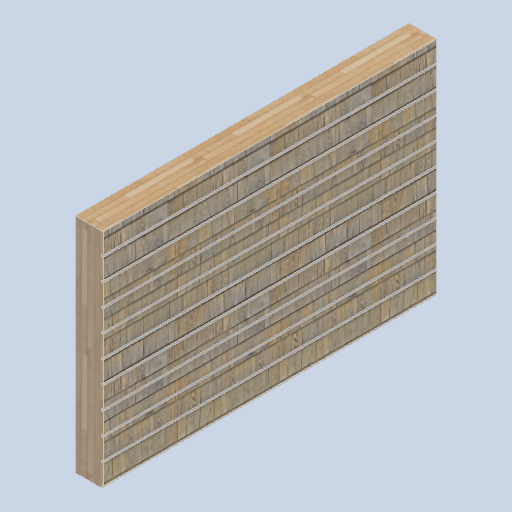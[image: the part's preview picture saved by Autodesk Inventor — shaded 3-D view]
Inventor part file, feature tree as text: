
AUTODESK INVENTOR PART (.ipt)
format: ipt  version: 2024.2 (Build 282272000, 272)  size: 367,616 bytes
history: native  units: in
note: dims shown in document units (in); Inventor stores cm internally (conversion verified against a paired STEP export)
features: other x3, sketch x1
ambient origin geometry x8: Origin, YZ Plane, XZ Plane, XY Plane, X Axis, Y Axis, Z Axis, Center Point
bodies: Solid1 (feature_tree)
feature tree (4):
  other  "side_wall_block_01.ipt"
  other  "Solid1::side_wall_block_01.ipt"
  other  "TaggingFeature1"
  sketch  "Sketch1"  dims[d0=0.3937in]
